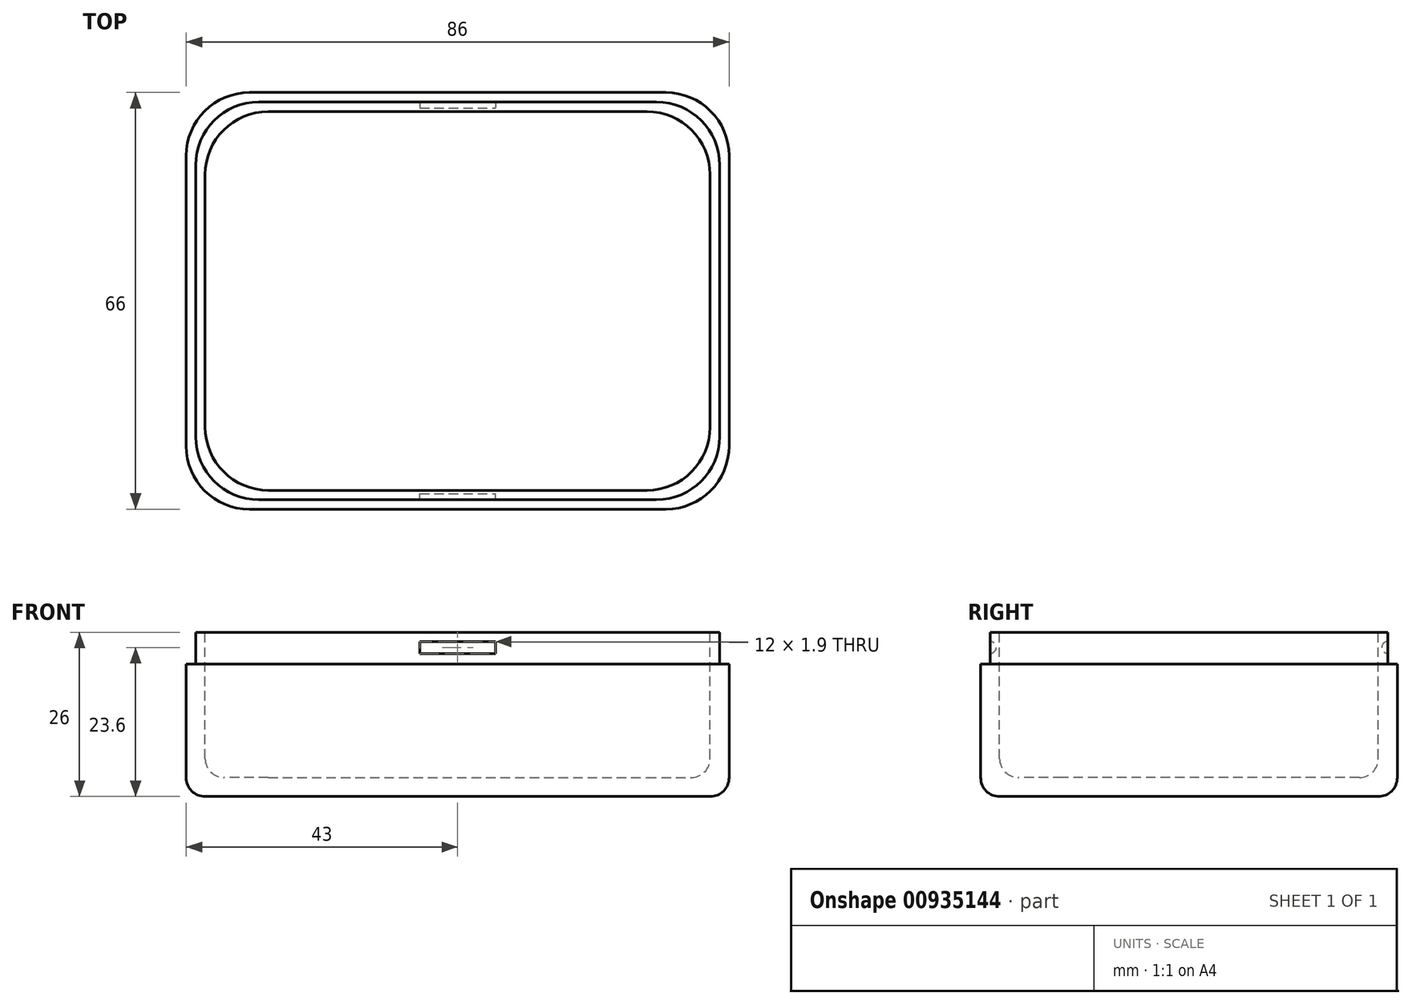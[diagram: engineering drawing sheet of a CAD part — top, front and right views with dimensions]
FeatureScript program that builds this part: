
annotation { "Feature Type Name" : "Feature", "Feature Type Description" : "" }
export const myFeature = defineFeature(function(context is Context, id is Id, definition is map)
    precondition{}
    {
        {
            var Q0;
            Q0=qCreatedBy(makeId("Top.planeOp"),FACE);
            var sketch = newSketch(context, id + "F0", { "sketchPlane" : qUnion([Q0])});
            skLineSegment(sketch, "E0.bottom", {"start": v(10, 0) * mm, "end": v(76, 0) * mm});
            skLineSegment(sketch, "E0.top", {"start": v(10, -66) * mm, "end": v(76, -66) * mm});
            skLineSegment(sketch, "E0.left", {"start": v(0, -10) * mm, "end": v(0, -56) * mm});
            skLineSegment(sketch, "E0.right", {"start": v(86, -10) * mm, "end": v(86, -56) * mm});
            skPoint(sketch, "E1.visualSharp", {"position": v(0, 0) * mm});
            skArc(sketch, "E1.filletArc", {"start": v(10, 0) * mm, "mid": v(2.93, -2.93) * mm, "end": v(0, -10) * mm});
            skPoint(sketch, "E2.visualSharp", {"position": v(86, 0) * mm});
            skArc(sketch, "E2.filletArc", {"start": v(86, -10) * mm, "mid": v(83.07, -2.93) * mm, "end": v(76, 0) * mm});
            skPoint(sketch, "E3.visualSharp", {"position": v(86, -66) * mm});
            skArc(sketch, "E3.filletArc", {"start": v(76, -66) * mm, "mid": v(83.07, -63.07) * mm, "end": v(86, -56) * mm});
            skPoint(sketch, "E4.visualSharp", {"position": v(0, -66) * mm});
            skArc(sketch, "E4.filletArc", {"start": v(0, -56) * mm, "mid": v(2.93, -63.07) * mm, "end": v(10, -66) * mm});
            skSolve(sketch);
        }
        {
            var Q0;
            Q0=qSketchRegion(id+"F0",true);
            extrude(context, id + "F1", {"entities" : qUnion([Q0]), "depth" : 26 * mm, "offsetDistance" : 25.4 * mm});
        }
        {
            var Q0;
            Q0=makeQuery(id+"F1.opExtrude","CAP_FACE",FACE,{"disambiguationData":[OSD([sQuery(id+"F0.wireOp",EDGE,"E0.bottom"),sQuery(id+"F0.wireOp",EDGE,"E0.top"),sQuery(id+"F0.wireOp",EDGE,"E0.left"),sQuery(id+"F0.wireOp",EDGE,"E0.right")])],"isStart":false});
            var sketch = newSketch(context, id + "F2", { "sketchPlane" : qUnion([Q0])});
            skLineSegment(sketch, "E5.bottom", {"start": v(13, -3) * mm, "end": v(73, -3) * mm});
            skLineSegment(sketch, "E5.top", {"start": v(13, -63) * mm, "end": v(73, -63) * mm});
            skLineSegment(sketch, "E5.left", {"start": v(3, -13) * mm, "end": v(3, -53) * mm});
            skLineSegment(sketch, "E5.right", {"start": v(83, -13) * mm, "end": v(83, -53) * mm});
            skPoint(sketch, "E6.visualSharp", {"position": v(3, -3) * mm});
            skArc(sketch, "E6.filletArc", {"start": v(13, -3) * mm, "mid": v(5.93, -5.93) * mm, "end": v(3, -13) * mm});
            skPoint(sketch, "E7.visualSharp", {"position": v(83, -3) * mm});
            skArc(sketch, "E7.filletArc", {"start": v(83, -13) * mm, "mid": v(80.07, -5.93) * mm, "end": v(73, -3) * mm});
            skPoint(sketch, "E8.visualSharp", {"position": v(83, -63) * mm});
            skArc(sketch, "E8.filletArc", {"start": v(73, -63) * mm, "mid": v(80.07, -60.07) * mm, "end": v(83, -53) * mm});
            skPoint(sketch, "E9.visualSharp", {"position": v(3, -63) * mm});
            skArc(sketch, "E9.filletArc", {"start": v(3, -53) * mm, "mid": v(5.93, -60.07) * mm, "end": v(13, -63) * mm});
            skSolve(sketch);
        }
        {
            var Q0;
            Q0=qSketchRegion(id+"F2",true);
            extrude(context, id + "F3", {"entities" : qUnion([Q0]), "operationType" : NewBodyOperationType.REMOVE, "oppositeDirection" : true, "depth" : 23 * mm, "offsetDistance" : 25.4 * mm});
        }
        {
            var Q0;
            Q0=makeQuery(id+"F1.opExtrude","CAP_FACE",FACE,{"disambiguationData":[OSD([sQuery(id+"F0.wireOp",EDGE,"E0.bottom"),sQuery(id+"F0.wireOp",EDGE,"E0.top"),sQuery(id+"F0.wireOp",EDGE,"E0.left"),sQuery(id+"F0.wireOp",EDGE,"E0.right")])],"isStart":false});
            var sketch = newSketch(context, id + "F4", { "sketchPlane" : qUnion([Q0])});
            skLineSegment(sketch, "E10.bottom", {"start": v(11.5, -1.5) * mm, "end": v(74.5, -1.5) * mm});
            skLineSegment(sketch, "E10.top", {"start": v(11.5, -64.5) * mm, "end": v(74.5, -64.5) * mm});
            skLineSegment(sketch, "E10.left", {"start": v(1.5, -11.5) * mm, "end": v(1.5, -54.5) * mm});
            skLineSegment(sketch, "E10.right", {"start": v(84.5, -11.5) * mm, "end": v(84.5, -54.5) * mm});
            skLineSegment(sketch, "E11.bottom", {"start": v(0, 0) * mm, "end": v(86, 0) * mm});
            skLineSegment(sketch, "E11.top", {"start": v(0, -66) * mm, "end": v(86, -66) * mm});
            skLineSegment(sketch, "E11.left", {"start": v(0, 0) * mm, "end": v(0, -66) * mm});
            skLineSegment(sketch, "E11.right", {"start": v(86, 0) * mm, "end": v(86, -66) * mm});
            skPoint(sketch, "E12.visualSharp", {"position": v(1.5, -1.5) * mm});
            skArc(sketch, "E12.filletArc", {"start": v(11.5, -1.5) * mm, "mid": v(4.43, -4.43) * mm, "end": v(1.5, -11.5) * mm});
            skPoint(sketch, "E13.visualSharp", {"position": v(84.5, -1.5) * mm});
            skArc(sketch, "E13.filletArc", {"start": v(84.5, -11.5) * mm, "mid": v(81.57, -4.43) * mm, "end": v(74.5, -1.5) * mm});
            skPoint(sketch, "E14.visualSharp", {"position": v(84.5, -64.5) * mm});
            skArc(sketch, "E14.filletArc", {"start": v(74.5, -64.5) * mm, "mid": v(81.57, -61.57) * mm, "end": v(84.5, -54.5) * mm});
            skPoint(sketch, "E15.visualSharp", {"position": v(1.5, -64.5) * mm});
            skArc(sketch, "E15.filletArc", {"start": v(1.5, -54.5) * mm, "mid": v(4.43, -61.57) * mm, "end": v(11.5, -64.5) * mm});
            skSolve(sketch);
        }
        {
            var Q0;
            Q0=qSketchRegion(id+"F4",true);
            extrude(context, id + "F5", {"entities" : qUnion([Q0]), "operationType" : NewBodyOperationType.REMOVE, "oppositeDirection" : true, "depth" : 5 * mm, "offsetDistance" : 25.4 * mm});
        }
        {
            var Q0;
            Q0=makeQuery(id+"F1.opExtrude","CAP_EDGE",EDGE,{"disambiguationData":[OSD([sQuery(id+"F0.wireOp",EDGE,"E2.filletArc")])],"isStart":true});
            var Q1;
            Q1=makeQuery(id+"F1.opExtrude","CAP_EDGE",EDGE,{"disambiguationData":[OSD([sQuery(id+"F0.wireOp",EDGE,"E0.bottom")])],"isStart":true});
            var Q2;
            Q2=makeQuery(id+"F1.opExtrude","CAP_EDGE",EDGE,{"disambiguationData":[OSD([sQuery(id+"F0.wireOp",EDGE,"E1.filletArc")])],"isStart":true});
            var Q3;
            Q3=makeQuery(id+"F1.opExtrude","CAP_EDGE",EDGE,{"disambiguationData":[OSD([sQuery(id+"F0.wireOp",EDGE,"E0.left")])],"isStart":true});
            var Q4;
            Q4=makeQuery(id+"F1.opExtrude","CAP_EDGE",EDGE,{"disambiguationData":[OSD([sQuery(id+"F0.wireOp",EDGE,"E4.filletArc")])],"isStart":true});
            var Q5;
            Q5=makeQuery(id+"F1.opExtrude","CAP_EDGE",EDGE,{"disambiguationData":[OSD([sQuery(id+"F0.wireOp",EDGE,"E0.top")])],"isStart":true});
            var Q6;
            Q6=makeQuery(id+"F1.opExtrude","CAP_EDGE",EDGE,{"disambiguationData":[OSD([sQuery(id+"F0.wireOp",EDGE,"E3.filletArc")])],"isStart":true});
            var Q7;
            Q7=makeQuery(id+"F1.opExtrude","CAP_EDGE",EDGE,{"disambiguationData":[OSD([sQuery(id+"F0.wireOp",EDGE,"E0.right")])],"isStart":true});
            fillet(context, id + "F6", {"entities" : qUnion([Q0, Q1, Q2, Q3, Q4, Q5, Q6, Q7]), "radius" : 3 * mm, "tangentPropagation" : true, "allowEdgeOverflow" : false});
        }
        {
            var Q0;
            Q0=makeQuery(id+"F3.boolean.opBoolean","COPY",FACE,{"derivedFrom":makeQuery(id+"F3.opExtrude","CAP_FACE",FACE,{"disambiguationData":[OSD([sQuery(id+"F2.wireOp",EDGE,"E5.bottom"),sQuery(id+"F2.wireOp",EDGE,"E5.top"),sQuery(id+"F2.wireOp",EDGE,"E5.left"),sQuery(id+"F2.wireOp",EDGE,"E5.right"),sQuery(id+"F2.wireOp",EDGE,"E6.filletArc"),sQuery(id+"F2.wireOp",EDGE,"E7.filletArc"),sQuery(id+"F2.wireOp",EDGE,"E8.filletArc"),sQuery(id+"F2.wireOp",EDGE,"E9.filletArc")])],"isStart":false})});
            fillet(context, id + "F7", {"entities" : qUnion([Q0]), "radius" : 3 * mm, "tangentPropagation" : true, "allowEdgeOverflow" : false});
        }
        {
            var Q0;
            Q0=qCreatedBy(makeId("Right.planeOp"),FACE);
            cPlane(context, id + "F8", {"entities" : qUnion([Q0]), "cplaneType" : CPlaneType.OFFSET, "offset" : 43 * mm, "width" : 150 * mm, "height" : 150 * mm});
        }
        {
            var Q0;
            Q0=qCreatedBy(id+"F8.planeOp",FACE);
            var sketch = newSketch(context, id + "F9", { "sketchPlane" : qUnion([Q0])});
            skCircle(sketch, "E16", {"center": v(-1.5, 23.6) * mm, "radius": 0.95 * mm});
            skLineSegment(sketch, "E17", {"start": v(-33, 37.43) * mm, "end": v(-33, -14.08) * mm, "construction": true});
            skCircle(sketch, "E18.MirrorC", {"center": v(-64.5, 23.6) * mm, "radius": 0.95 * mm});
            skSolve(sketch);
        }
        {
            var Q0;
            Q0 = qSketchRegion(id + "F9", true);
            extrude(context, id + "F10", {"entities" : qUnion([Q0]), "operationType" : NewBodyOperationType.REMOVE, "endBound" : BoundingType.SYMMETRIC, "oppositeDirection" : true, "depth" : 12 * mm, "offsetDistance" : 25 * mm});
        }
    });
